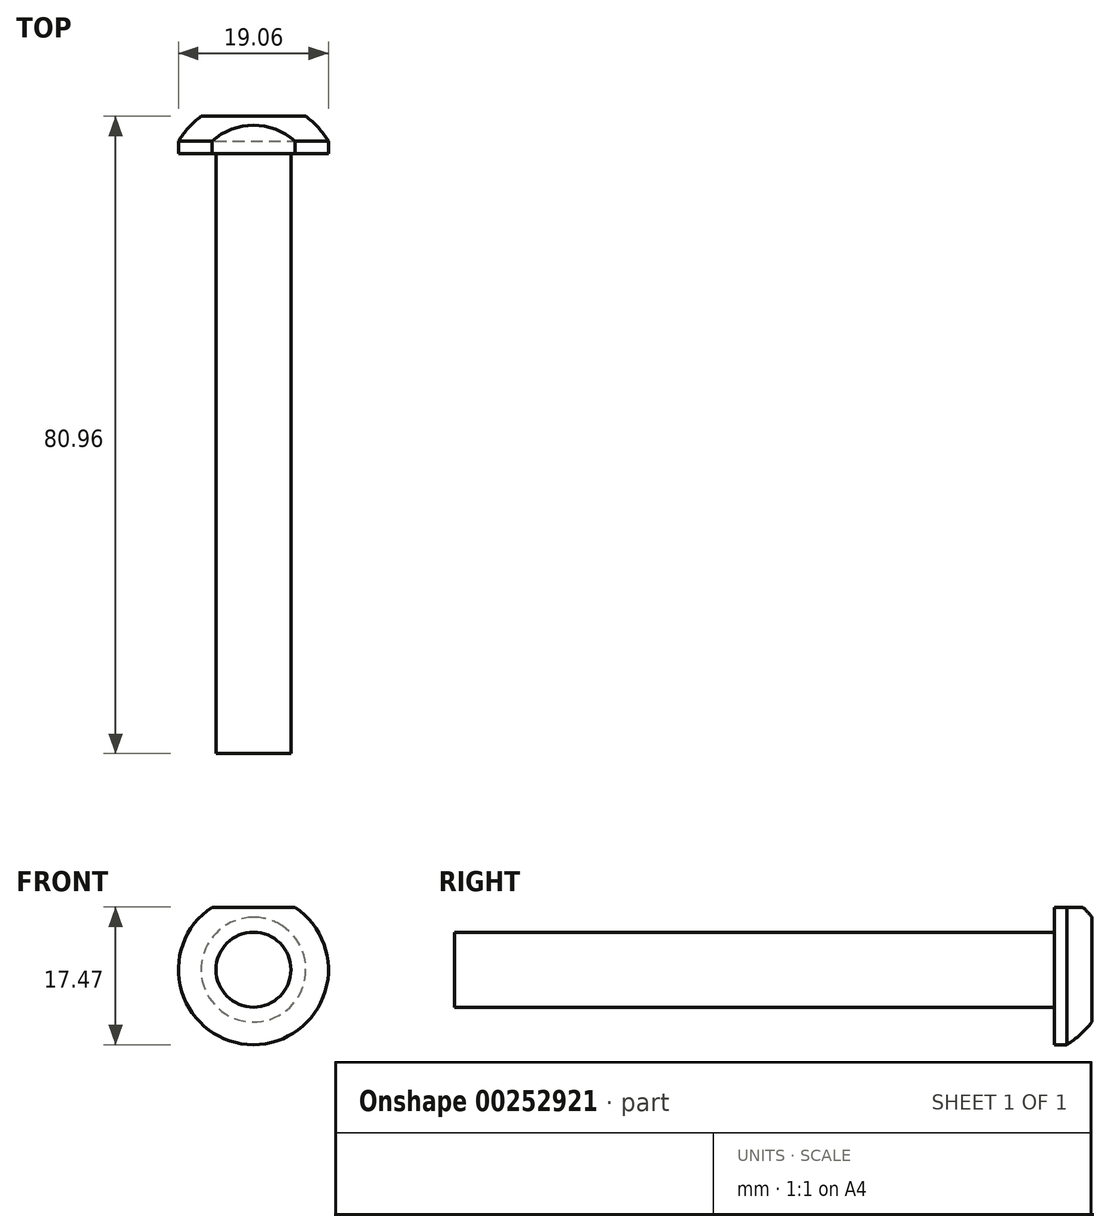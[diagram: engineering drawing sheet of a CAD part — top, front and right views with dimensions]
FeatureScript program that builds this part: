
annotation { "Feature Type Name" : "Feature", "Feature Type Description" : "" }
export const myFeature = defineFeature(function(context is Context, id is Id, definition is map)
    precondition{}
    {
        {
            var Q0;
            Q0=qCreatedBy(makeId("Front.planeOp"),FACE);
            var sketch = newSketch(context, id + "F0", { "sketchPlane" : qUnion([Q0])});
            skCircle(sketch, "E0", {"center": v(0, 0) * mm, "radius": 4.76 * mm});
            skSolve(sketch);
        }
        {
            var Q0;
            Q0 = qSketchRegion(id + "F0", true);
            extrude(context, id + "F1", {"entities" : qUnion([Q0]), "depth" : 76.2 * mm});
        }
        {
            var Q0;
            Q0=qCreatedBy(makeId("Right.planeOp"),FACE);
            var sketch = newSketch(context, id + "F2", { "sketchPlane" : qUnion([Q0])});
            skLineSegment(sketch, "E1", {"start": v(0, 0) * mm, "end": v(0, 9.53) * mm});
            skLineSegment(sketch, "E2", {"start": v(0, 9.53) * mm, "end": v(1.59, 9.53) * mm});
            skArc(sketch, "E3", {"start": v(6.97, 0) * mm, "mid": v(5.53, 5.47) * mm, "end": v(1.58, 9.53) * mm});
            skLineSegment(sketch, "E4", {"start": v(0, 0) * mm, "end": v(6.97, 0) * mm});
            skSolve(sketch);
        }
        {
            var Q0;
            Q0 = qSketchRegion(id + "F2", true);
            var Q1;
            Q1=sQuery(id+"F2.wireOp",EDGE,"E4");
            revolve(context, id + "F3", {"operationType" : NewBodyOperationType.ADD, "entities" : qUnion([Q0]), "axis" : qUnion([Q1]), "revolveType" : RevolveType.FULL});
        }
        {
            var Q0;
            Q0=qCreatedBy(makeId("Right.planeOp"),FACE);
            var sketch = newSketch(context, id + "F4", { "sketchPlane" : qUnion([Q0])});
            skLineSegment(sketch, "E5", {"start": v(0, 0) * mm, "end": v(4.76, 0) * mm, "construction": true});
            skLineSegment(sketch, "E6", {"start": v(4.76, 0) * mm, "end": v(4.76, 8) * mm});
            skLineSegment(sketch, "E7", {"start": v(4.76, 8) * mm, "end": v(8.82, 8) * mm});
            skLineSegment(sketch, "E8", {"start": v(8.82, 8) * mm, "end": v(8.82, -11.38) * mm});
            skLineSegment(sketch, "E9", {"start": v(4.76, 0) * mm, "end": v(4.76, -11.38) * mm});
            skLineSegment(sketch, "E10", {"start": v(8.82, -11.38) * mm, "end": v(4.76, -11.38) * mm});
            skSolve(sketch);
        }
        {
            var Q0;
            Q0 = qSketchRegion(id + "F4", true);
            extrude(context, id + "F5", {"entities" : qUnion([Q0]), "operationType" : NewBodyOperationType.REMOVE, "oppositeDirection" : true, "depth" : 25.4 * mm, "hasSecondDirection" : true, "secondDirectionOppositeDirection" : false, "secondDirectionDepth" : 25.4 * mm});
        }
        {
            var Q0;
            Q0=qCreatedBy(makeId("Front.planeOp"),FACE);
            var sketch = newSketch(context, id + "F6", { "sketchPlane" : qUnion([Q0])});
            skLineSegment(sketch, "E11", {"start": v(0, 0) * mm, "end": v(0, 7.94) * mm});
            skLineSegment(sketch, "E12", {"start": v(0, 7.94) * mm, "end": v(-8.75, 7.94) * mm});
            skLineSegment(sketch, "E13", {"start": v(-8.75, 7.94) * mm, "end": v(-8.75, 11.57) * mm});
            skLineSegment(sketch, "E14", {"start": v(-8.75, 11.57) * mm, "end": v(10.3, 11.57) * mm});
            skLineSegment(sketch, "E15", {"start": v(0, 7.94) * mm, "end": v(10.3, 7.94) * mm});
            skLineSegment(sketch, "E16", {"start": v(10.3, 7.94) * mm, "end": v(10.3, 11.57) * mm});
            skSolve(sketch);
        }
        {
            var Q0;
            Q0 = qSketchRegion(id + "F6", true);
            extrude(context, id + "F7", {"entities" : qUnion([Q0]), "operationType" : NewBodyOperationType.REMOVE, "oppositeDirection" : true, "depth" : 25.4 * mm});
        }
    });
